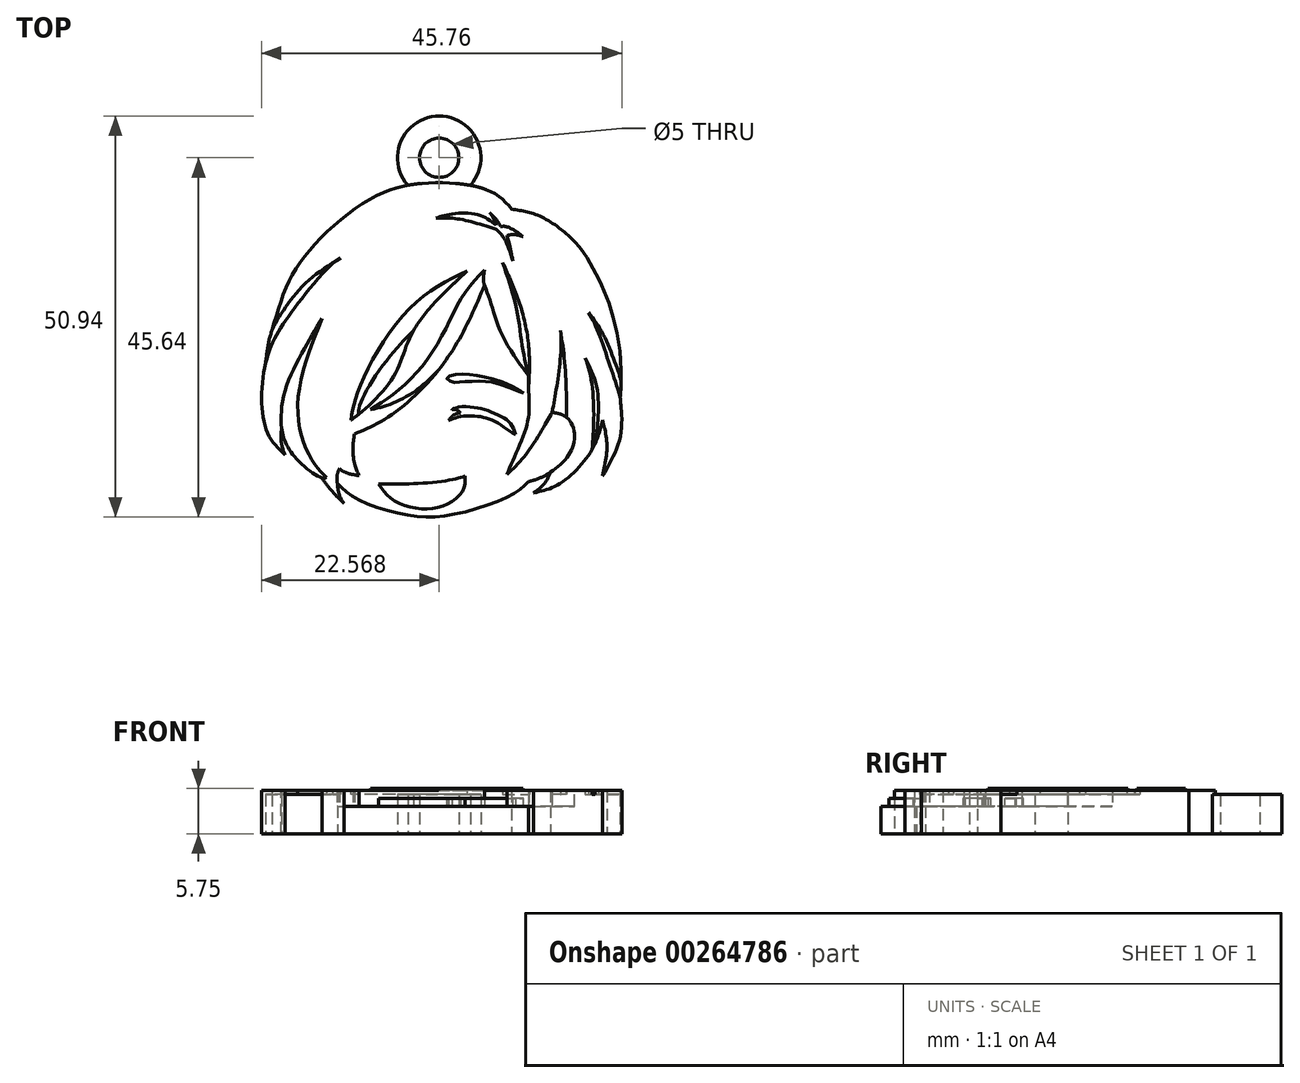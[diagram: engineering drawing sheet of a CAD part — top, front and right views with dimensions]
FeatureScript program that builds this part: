
annotation { "Feature Type Name" : "Feature", "Feature Type Description" : "" }
export const myFeature = defineFeature(function(context is Context, id is Id, definition is map)
    precondition{}
    {
        {
            var Q0;
            Q0=qCreatedBy(makeId("Top.planeOp"),FACE);
            var sketch = newSketch(context, id + "F0", { "sketchPlane" : qUnion([Q0])});
            skLineSegment(sketch, "E0", {"start": v(0, 25.68) * mm, "end": v(0, -14.32) * mm, "construction": true});
            skFitSpline(sketch, "E1", {"points": [v(-12.11, -11) * mm, v(-9.76, -12.87) * mm, v(-3.35, -15) * mm, v(2.65, -14.93) * mm, v(10, -12.46) * mm, v(12.18, -10.76) * mm], "startDerivative": vector(12.35, -12.38) * mm, "endDerivative": vector(10.78, 11.62) * mm});
            skFitSpline(sketch, "E2", {"points": [v(12.18, -10.76) * mm, v(14.09, -10.08) * mm, v(16.86, -7.95) * mm, v(18.04, -4.98) * mm, v(17, -2.6) * mm, v(15.17, -1.96) * mm], "startDerivative": vector(10.79, 2.75) * mm, "endDerivative": vector(-11.46, 1.84) * mm});
            skFitSpline(sketch, "E3", {"points": [v(15.17, -1.96) * mm, v(13.89, -4.19) * mm, v(11.42, -7.85) * mm, v(9.44, -9.83) * mm], "startDerivative": vector(-3.84, -6.82) * mm, "endDerivative": vector(-6.23, -5.5) * mm});
            skFitSpline(sketch, "E4", {"points": [v(-12.11, -11) * mm, v(-12.11, -9.83) * mm, v(-11.84, -9.1) * mm], "startDerivative": vector(-0.17, 2.25) * mm, "endDerivative": vector(0.73, 1.5) * mm});
            skFitSpline(sketch, "E5", {"points": [v(-11.84, -9.1) * mm, v(-11.03, -9.62) * mm, v(-9.33, -10) * mm], "startDerivative": vector(1.68, -1.34) * mm, "endDerivative": vector(3.28, -0.49) * mm});
            skFitSpline(sketch, "E6", {"points": [v(-9.33, -10) * mm, v(-9.85, -8.77) * mm, v(-10.14, -6.57) * mm, v(-9.93, -4.7) * mm], "startDerivative": vector(-1.97, 3.85) * mm, "endDerivative": vector(0.9, 5.24) * mm});
            skFitSpline(sketch, "E7", {"points": [v(-9.93, -4.7) * mm, v(-7.03, -3.4) * mm, v(-2.43, 0) * mm, v(2.7, 6.2) * mm, v(6.59, 14.18) * mm], "startDerivative": vector(15.57, 6.03) * mm, "endDerivative": vector(11.78, 27.65) * mm});
            skFitSpline(sketch, "E8", {"points": [v(6.59, 14.18) * mm, v(7.53, 11.45) * mm, v(9.07, 7.36) * mm, v(11.76, 3.27) * mm, v(12.18, 2.67) * mm], "startDerivative": vector(3.84, -10.5) * mm, "endDerivative": vector(1.51, -3.88) * mm});
            skFitSpline(sketch, "E9", {"points": [v(12.18, 2.67) * mm, v(12.18, 1.06) * mm, v(12.26, -1.4) * mm, v(11.85, -3.97) * mm, v(10.55, -7.25) * mm, v(9.44, -9.83) * mm], "startDerivative": vector(-0.17, -13.3) * mm, "endDerivative": vector(-4.42, -10.34) * mm});
            skFitSpline(sketch, "E10", {"points": [v(-12.11, -11) * mm, v(-11.84, -12.48) * mm, v(-11.26, -13.55) * mm], "startDerivative": vector(0.32, -2.98) * mm, "endDerivative": vector(1.41, -2.12) * mm});
            skFitSpline(sketch, "E11", {"points": [v(-11.26, -13.55) * mm, v(-13.1, -11.63) * mm, v(-14.07, -10.3) * mm], "startDerivative": vector(-3.59, 3.55) * mm, "endDerivative": vector(-1.98, 2.94) * mm});
            skFitSpline(sketch, "E12", {"points": [v(-14.05, 9.94) * mm, v(-16.53, 3.07) * mm, v(-17.07, -2.82) * mm, v(-15.88, -7.02) * mm, v(-14.56, -9.1) * mm, v(-13.47, -10.23) * mm], "startDerivative": vector(-10.57, -25.7) * mm, "endDerivative": vector(8.74, -8.35) * mm});
            skFitSpline(sketch, "E13", {"points": [v(-13.47, -10.23) * mm, v(-14.07, -10.3) * mm, v(-17.06, -8.13) * mm, v(-18.78, -5.57) * mm, v(-19.25, -3.19) * mm, v(-18.7, 0.95) * mm, v(-16.23, 6.25) * mm, v(-14.05, 9.94) * mm], "startDerivative": vector(-7.9, -3.21) * mm, "endDerivative": vector(12.69, 21.1) * mm});
            skFitSpline(sketch, "E14", {"points": [v(-19.19, -3.98) * mm, v(-19.27, -5.57) * mm, v(-18.78, -7.39) * mm], "startDerivative": vector(-0.4, -3.27) * mm, "endDerivative": vector(1.14, -3.48) * mm});
            skFitSpline(sketch, "E15", {"points": [v(-18.78, -7.39) * mm, v(-20.4, -5.57) * mm, v(-21.53, -2.66) * mm, v(-21.58, 2.24) * mm, v(-20.43, 6.68) * mm, v(-18.3, 10.23) * mm, v(-12.7, 16.96) * mm], "startDerivative": vector(-13.06, 14.6) * mm, "endDerivative": vector(30.17, 28.96) * mm});
            skFitSpline(sketch, "E16", {"points": [v(-12.7, 16.96) * mm, v(-11.7, 17.65) * mm], "startDerivative": vector(1, 0.69) * mm, "endDerivative": vector(1, 0.69) * mm});
            skFitSpline(sketch, "E17", {"points": [v(-11.7, 17.65) * mm, v(-16.11, 14.49) * mm, v(-18.94, 11) * mm, v(-20.52, 8.12) * mm, v(-21.21, 4.3) * mm], "startDerivative": vector(-16.65, -10.4) * mm, "endDerivative": vector(-1.83, -16.87) * mm});
            skFitSpline(sketch, "E18", {"points": [v(-20.38, 8.5) * mm, v(-18.48, 14.22) * mm, v(-15.07, 19.27) * mm, v(-8.42, 24.86) * mm, v(-2.6, 26.98) * mm, v(3.7, 27.04) * mm, v(7.93, 25.8) * mm, v(10.05, 23.86) * mm], "startDerivative": vector(11.29, 40.08) * mm, "endDerivative": vector(18.3, -20.86) * mm});
            skFitSpline(sketch, "E19", {"points": [v(10.05, 23.86) * mm, v(13.67, 22.93) * mm, v(18.22, 19.5) * mm, v(20.87, 15.37) * mm, v(22.83, 10.48) * mm, v(23.82, 0) * mm], "startDerivative": vector(22, -3.37) * mm, "endDerivative": vector(-4.69, -45.16) * mm});
            skFitSpline(sketch, "E20", {"points": [v(15, -9.56) * mm, v(14.09, -11.14) * mm, v(12.83, -12.19) * mm], "startDerivative": vector(-1.55, -3.32) * mm, "endDerivative": vector(-2.78, -1.93) * mm});
            skFitSpline(sketch, "E21", {"points": [v(12.83, -12.19) * mm, v(16.19, -11) * mm, v(20.25, -6.66) * mm, v(21.57, -2.95) * mm], "startDerivative": vector(10.98, 2.3) * mm, "endDerivative": vector(2.75, 11.42) * mm});
            skFitSpline(sketch, "E22", {"points": [v(21.57, -2.95) * mm, v(22.13, -6.17) * mm, v(21.57, -10.08) * mm], "startDerivative": vector(1.7, -6.59) * mm, "endDerivative": vector(-1.66, -7.64) * mm});
            skFitSpline(sketch, "E23", {"points": [v(5.07, 16.64) * mm, v(-2.43, 8.44) * mm, v(-5, 2.57) * mm, v(-10.38, -2.95) * mm, v(-14.16, -5.13) * mm], "startDerivative": vector(-29, -26.73) * mm, "endDerivative": vector(-18.26, -9.03) * mm});
            skFitSpline(sketch, "E24", {"points": [v(-14.16, -5.13) * mm, v(-11.64, -5.13) * mm, v(-9.93, -4.7) * mm], "startDerivative": vector(4.87, -0.26) * mm, "endDerivative": vector(3.55, 1.17) * mm});
            skFitSpline(sketch, "E25", {"points": [v(-2.43, 8.44) * mm, v(-4.37, 6.4) * mm, v(-8.03, 1.5) * mm, v(-9.36, -1.47) * mm, v(-9.44, -2.24) * mm], "startDerivative": vector(-7.12, -7.14) * mm, "endDerivative": vector(-0.06, -5.2) * mm});
            skFitSpline(sketch, "E26", {"points": [v(16.06, 10.25) * mm, v(16.3, 6.6) * mm, v(15.81, 1.7) * mm, v(15.17, -1.96) * mm], "startDerivative": vector(1.27, -11.01) * mm, "endDerivative": vector(-2.04, -10.92) * mm});
            skFitSpline(sketch, "E27", {"points": [v(17, -2.6) * mm, v(17, -0.67) * mm, v(16.78, 4.23) * mm, v(16.25, 8.44) * mm], "startDerivative": vector(0.07, 6.87) * mm, "endDerivative": vector(-1.64, 10.96) * mm});
            skFitSpline(sketch, "E28", {"points": [v(23.82, 0) * mm, v(22.51, 4) * mm, v(20.95, 8.44) * mm, v(19.8, 10.74) * mm], "startDerivative": vector(-3.08, 11) * mm, "endDerivative": vector(-4.1, 7.49) * mm});
            skFitSpline(sketch, "E29", {"points": [v(19.8, 10.74) * mm, v(21.57, 8.1) * mm, v(23.16, 4.36) * mm, v(23.95, 2.03) * mm], "startDerivative": vector(5.44, -7.3) * mm, "endDerivative": vector(1.84, -7.43) * mm});
            skFitSpline(sketch, "E30", {"points": [v(8.87, 17.05) * mm, v(10.55, 11.64) * mm, v(11.4, 6.35) * mm, v(12.18, 2.67) * mm], "startDerivative": vector(5.33, -14.86) * mm, "endDerivative": vector(2.88, -11.93) * mm});
            skFitSpline(sketch, "E31", {"points": [v(8.87, 17.05) * mm, v(10.87, 12.37) * mm, v(12.18, 6.63) * mm, v(12.18, 1.06) * mm], "startDerivative": vector(6.63, -14.09) * mm, "endDerivative": vector(-0.84, -16.47) * mm});
            skFitSpline(sketch, "E32", {"points": [v(18.48, 6.7) * mm, v(19.8, 3.68) * mm, v(20.46, -1.96) * mm, v(20.25, -6.66) * mm], "startDerivative": vector(5.18, -9.46) * mm, "endDerivative": vector(-1.03, -13.13) * mm});
            skFitSpline(sketch, "E33", {"points": [v(4.37, 15.98) * mm, v(-3.02, 11.16) * mm, v(-9.36, 1.06) * mm, v(-10.38, -2.95) * mm], "startDerivative": vector(-21.56, -10.26) * mm, "endDerivative": vector(-2.26, -14.44) * mm});
            skFitSpline(sketch, "E34", {"points": [v(6.59, 14.18) * mm, v(6.45, 14.79) * mm, v(6.59, 16.15) * mm], "startDerivative": vector(-0.47, 1.35) * mm, "endDerivative": vector(0.42, 2.5) * mm});
            skFitSpline(sketch, "E35", {"points": [v(6.59, 16.15) * mm, v(3.98, 13.05) * mm, v(1.6, 8.58) * mm, v(-1.53, 3.65) * mm, v(-5.07, 0.3) * mm, v(-7.86, -1.63) * mm], "startDerivative": vector(-14.68, -15.38) * mm, "endDerivative": vector(-15.93, -10.28) * mm});
            skFitSpline(sketch, "E36", {"points": [v(-7.86, -1.63) * mm, v(-4.86, -0.72) * mm, v(-1.67, 1.17) * mm, v(0.73, 3.41) * mm], "startDerivative": vector(9.28, 2.26) * mm, "endDerivative": vector(6.78, 7.07) * mm});
            skFitSpline(sketch, "E37", {"points": [v(8.06, 21.84) * mm, v(5.77, 23.14) * mm, v(2.15, 23.2) * mm, v(0.21, 22.64) * mm], "startDerivative": vector(-6.2, 4.74) * mm, "endDerivative": vector(-5.99, -2.2) * mm});
            skFitSpline(sketch, "E38", {"points": [v(0.4, 22.7) * mm, v(3.04, 22.64) * mm, v(8, 21.34) * mm], "startDerivative": vector(5.84, 0.26) * mm, "endDerivative": vector(9.18, -2.82) * mm});
            skFitSpline(sketch, "E39", {"points": [v(8, 21.34) * mm, v(9.07, 20.14) * mm, v(10.18, 17.28) * mm], "startDerivative": vector(2.67, -2.44) * mm, "endDerivative": vector(1.73, -5.52) * mm});
            skFitSpline(sketch, "E40", {"points": [v(10.18, 17.28) * mm, v(9.71, 19.49) * mm, v(9.43, 20.49) * mm], "startDerivative": vector(-0.82, 4.07) * mm, "endDerivative": vector(-0.69, 2.22) * mm});
            skFitSpline(sketch, "E41", {"points": [v(9.43, 20.49) * mm, v(10.33, 20.64) * mm, v(11.45, 20.36) * mm], "startDerivative": vector(1.88, 0.5) * mm, "endDerivative": vector(2.16, -0.73) * mm});
            skFitSpline(sketch, "E42", {"points": [v(8.64, 21.65) * mm, v(9.43, 21.61) * mm, v(10.87, 20.85) * mm, v(11.45, 20.36) * mm], "startDerivative": vector(2.43, 0.26) * mm, "endDerivative": vector(1.67, -1.54) * mm});
            skFitSpline(sketch, "E43", {"points": [v(8.06, 21.84) * mm, v(7.74, 22.64) * mm, v(7.25, 23.4) * mm], "startDerivative": vector(-0.6, 1.63) * mm, "endDerivative": vector(-1.03, 1.5) * mm});
            skFitSpline(sketch, "E44", {"points": [v(7.25, 23.4) * mm, v(8.22, 22.33) * mm, v(8.64, 21.65) * mm], "startDerivative": vector(1.9, -1.95) * mm, "endDerivative": vector(0.83, -1.54) * mm});
            skFitSpline(sketch, "E45", {"points": [v(6.59, 16.15) * mm, v(4.45, 15.54) * mm, v(2.54, 14.27) * mm], "startDerivative": vector(-4.44, -0.9) * mm, "endDerivative": vector(-3.63, -2.88) * mm});
            skLineSegment(sketch, "E46", {"start": v(5.07, 16.64) * mm, "end": v(-6.25, 25.97) * mm});
            skLineSegment(sketch, "E47", {"start": v(11.74, 9.35) * mm, "end": v(16.06, 21.48) * mm});
            skFitSpline(sketch, "E48", {"points": [v(23.82, 0) * mm, v(23.88, -0.74) * mm, v(23.89, -4.73) * mm, v(21.57, -10.08) * mm], "startDerivative": vector(0.4, -7.14) * mm, "endDerivative": vector(-6.66, -11.4) * mm});
            skFitSpline(sketch, "E49", {"points": [v(16.06, 10.25) * mm, v(17.69, 8.1) * mm, v(18.48, 6.7) * mm], "startDerivative": vector(3.19, -3.97) * mm, "endDerivative": vector(1.58, -3.1) * mm});
            skFitSpline(sketch, "E50", {"points": [v(19.36, 4.94) * mm, v(20.77, 1.57) * mm, v(21, -2.9) * mm, v(20.59, -6) * mm], "startDerivative": vector(5.07, -9.54) * mm, "endDerivative": vector(-1.62, -9.52) * mm});
            skSolve(sketch);
        }
        {
            var Q0;
            Q0=makeQuery(id+"F0.imprint","IMPRINT",FACE,{"disambiguationData":[TD([[makeQuery(id+"F0.imprint","IMPRINT",EDGE,{"derivedFrom":sQuery(id+"F0.wireOp",EDGE,"E1")}),1.0]])]});
            var Q1;
            {var subQ0=sQuery(id+"F0.wireOp",EDGE,"E25");Q1=makeQuery(id+"F0.imprint","IMPRINT",FACE,{"disambiguationData":[TD([[makeQuery(id+"F0.imprint","IMPRINT",EDGE,{"derivedFrom":subQ0}),1.0]])]});}
            extrude(context, id + "F1", {"entities" : qUnion([Q0, Q1]), "depth" : 3.5 * mm, "offsetDistance" : 25 * mm});
        }
        {
            var Q0;
            {var subQ3=sQuery(id+"F0.wireOp",EDGE,"E27");Q0=makeQuery(id+"F0.imprint","IMPRINT",FACE,{"disambiguationData":[TD([[makeQuery(id+"F0.imprint","IMPRINT",EDGE,{"derivedFrom":subQ3}),1.0]])]});}
            var Q1;
            Q1=makeQuery(id+"F0.imprint","IMPRINT",FACE,{"disambiguationData":[TD([[makeQuery(id+"F0.imprint","IMPRINT",EDGE,{"derivedFrom":sQuery(id+"F0.wireOp",EDGE,"E32")}),1.0]])]});
            var Q2;
            {var subQ0=sQuery(id+"F0.wireOp",EDGE,"E28");Q2=makeQuery(id+"F0.imprint","IMPRINT",FACE,{"disambiguationData":[TD([[makeQuery(id+"F0.imprint","IMPRINT",EDGE,{"derivedFrom":subQ0}),-1.0]])]});}
            var Q3;
            {var subQ0=sQuery(id+"F0.wireOp",EDGE,"E12");Q3=makeQuery(id+"F0.imprint","IMPRINT",FACE,{"disambiguationData":[TD([[makeQuery(id+"F0.imprint","IMPRINT",EDGE,{"derivedFrom":subQ0}),-1.0]])]});}
            var Q4;
            {var subQ0=sQuery(id+"F0.wireOp",EDGE,"E16");Q4=makeQuery(id+"F0.imprint","IMPRINT",FACE,{"disambiguationData":[TD([[makeQuery(id+"F0.imprint","IMPRINT",EDGE,{"derivedFrom":subQ0}),1.0]])]});}
            var Q5;
            {var subQ0=sQuery(id+"F0.wireOp",EDGE,"E25");Q5=makeQuery(id+"F0.imprint","IMPRINT",FACE,{"disambiguationData":[TD([[makeQuery(id+"F0.imprint","IMPRINT",EDGE,{"derivedFrom":subQ0}),-1.0]])]});}
            var Q6;
            {var subQ0=sQuery(id+"F0.wireOp",EDGE,"E30");Q6=makeQuery(id+"F0.imprint","IMPRINT",FACE,{"disambiguationData":[TD([[makeQuery(id+"F0.imprint","IMPRINT",EDGE,{"derivedFrom":subQ0}),1.0]])]});}
            extrude(context, id + "F2", {"entities" : qUnion([Q0, Q1, Q2, Q3, Q4, Q5, Q6]), "operationType" : NewBodyOperationType.ADD, "depth" : 5 * mm, "offsetDistance" : 25 * mm});
        }
        {
            var Q0;
            {var subQ0=sQuery(id+"F0.wireOp",EDGE,"E34");Q0=makeQuery(id+"F0.imprint","IMPRINT",FACE,{"disambiguationData":[TD([[makeQuery(id+"F0.imprint","IMPRINT",EDGE,{"derivedFrom":subQ0}),1.0]])]});}
            extrude(context, id + "F3", {"entities" : qUnion([Q0]), "operationType" : NewBodyOperationType.ADD, "depth" : 5.75 * mm, "offsetDistance" : 25 * mm});
        }
        {
            var Q0;
            {var subQ6=sQuery(id+"F0.wireOp",EDGE,"E24");Q0=makeQuery(id+"F0.imprint","IMPRINT",FACE,{"disambiguationData":[TD([[makeQuery(id+"F0.imprint","IMPRINT",EDGE,{"derivedFrom":subQ6}),1.0]])]});}
            extrude(context, id + "F4", {"entities" : qUnion([Q0]), "depth" : 5.5 * mm, "offsetDistance" : 25 * mm});
        }
        {
            var Q0;
            {var subQ0=sQuery(id+"F0.wireOp",EDGE,"E38");Q0=makeQuery(id+"F0.imprint","IMPRINT",FACE,{"disambiguationData":[TD([[makeQuery(id+"F0.imprint","IMPRINT",EDGE,{"derivedFrom":subQ0}),1.0]])]});}
            extrude(context, id + "F5", {"entities" : qUnion([Q0]), "operationType" : NewBodyOperationType.ADD, "depth" : 5.75 * mm, "offsetDistance" : 25 * mm});
        }
        {
            var Q0;
            Q0=makeQuery(id+"F0.imprint","IMPRINT",FACE,{"disambiguationData":[TD([[makeQuery(id+"F0.imprint","IMPRINT",EDGE,{"derivedFrom":sQuery(id+"F0.wireOp",EDGE,"E4")}),1.0]])]});
            extrude(context, id + "F6", {"entities" : qUnion([Q0]), "operationType" : NewBodyOperationType.ADD, "depth" : 5.5 * mm, "offsetDistance" : 25 * mm});
        }
        {
            var Q0;
            Q0=makeQuery(id+"F0.imprint","IMPRINT",FACE,{"disambiguationData":[TD([[makeQuery(id+"F0.imprint","IMPRINT",EDGE,{"derivedFrom":sQuery(id+"F0.wireOp",EDGE,"E8")}),1.0]])]});
            extrude(context, id + "F7", {"entities" : qUnion([Q0]), "operationType" : NewBodyOperationType.ADD, "depth" : 5.5 * mm, "offsetDistance" : 25 * mm});
        }
        {
            var Q0;
            {var subQ4=sQuery(id+"F0.wireOp",EDGE,"E3");Q0=makeQuery(id+"F0.imprint","IMPRINT",FACE,{"disambiguationData":[TD([[makeQuery(id+"F0.imprint","IMPRINT",EDGE,{"derivedFrom":subQ4}),-1.0]])]});}
            extrude(context, id + "F8", {"entities" : qUnion([Q0]), "operationType" : NewBodyOperationType.ADD, "depth" : 5.5 * mm, "offsetDistance" : 25 * mm});
        }
        {
            var Q0;
            {var subQ1=sQuery(id+"F0.wireOp",EDGE,"E20");Q0=makeQuery(id+"F0.imprint","IMPRINT",FACE,{"disambiguationData":[TD([[makeQuery(id+"F0.imprint","IMPRINT",EDGE,{"derivedFrom":subQ1}),1.0]])]});}
            extrude(context, id + "F9", {"entities" : qUnion([Q0]), "operationType" : NewBodyOperationType.ADD, "depth" : 5.5 * mm, "offsetDistance" : 25 * mm});
        }
        {
            var Q0;
            Q0=qCreatedBy(makeId("Top.planeOp"),FACE);
            var sketch = newSketch(context, id + "F10", { "sketchPlane" : qUnion([Q0])});
            skFitSpline(sketch, "E51", {"points": [v(-6.88, -11.06) * mm, v(-3.04, -11.06) * mm, v(2.25, -10.56) * mm, v(4.14, -10.06) * mm], "startDerivative": vector(10.2, -0.25) * mm, "endDerivative": vector(6.46, 2.11) * mm});
            skFitSpline(sketch, "E52", {"points": [v(-6.88, -11.06) * mm, v(-5.13, -13) * mm, v(-1.7, -14.2) * mm, v(1.75, -13.7) * mm, v(3.84, -11.86) * mm, v(4.14, -10.06) * mm], "startDerivative": vector(7.65, -10.93) * mm, "endDerivative": vector(0.06, 11.32) * mm});
            skFitSpline(sketch, "E53", {"points": [v(3.53, -2.02) * mm, v(2.77, -2.23) * mm, v(2.02, -2.98) * mm], "startDerivative": vector(-1.69, -0.24) * mm, "endDerivative": vector(-1.34, -1.66) * mm});
            skFitSpline(sketch, "E54", {"points": [v(2.02, -2.98) * mm, v(3.57, -2.5) * mm, v(5.48, -2.44) * mm, v(7.61, -2.98) * mm, v(10.15, -4.6) * mm], "startDerivative": vector(6.93, 2.62) * mm, "endDerivative": vector(8.63, -6.27) * mm});
            skFitSpline(sketch, "E55", {"points": [v(3.53, -2.02) * mm, v(2.96, -1.62) * mm, v(2.44, -1.64) * mm], "startDerivative": vector(-1.04, 0.96) * mm, "endDerivative": vector(-1.14, -0.23) * mm});
            skFitSpline(sketch, "E56", {"points": [v(2.44, -1.64) * mm, v(3.27, -1.3) * mm, v(5.43, -1.35) * mm, v(7.28, -1.85) * mm, v(9.02, -2.67) * mm, v(9.92, -3.44) * mm, v(10.55, -4.8) * mm], "startDerivative": vector(5.57, 3.15) * mm, "endDerivative": vector(3.4, -9.15) * mm});
            skFitSpline(sketch, "E57", {"points": [v(10.15, -4.6) * mm, v(10.55, -4.8) * mm], "startDerivative": vector(0.4, -0.2) * mm, "endDerivative": vector(0.4, -0.2) * mm});
            skFitSpline(sketch, "E58", {"points": [v(11.5, 0.5) * mm, v(8.85, 1.91) * mm, v(5.23, 2.74) * mm, v(2.82, 2.83) * mm, v(1.82, 2.33) * mm, v(2.52, 1.87) * mm, v(3.69, 1.91) * mm, v(5.98, 2) * mm, v(8.35, 1.66) * mm, v(11.5, 0.5) * mm]});
            skSolve(sketch);
        }
        {
            var Q0;
            Q0 = qSketchRegion(id + "F10", true);
            extrude(context, id + "F11", {"entities" : qUnion([Q0]), "operationType" : NewBodyOperationType.ADD, "depth" : 4.5 * mm, "offsetDistance" : 25 * mm});
        }
        {
            var Q0;
            Q0=qCreatedBy(makeId("Top.planeOp"),FACE);
            var sketch = newSketch(context, id + "F12", { "sketchPlane" : qUnion([Q0])});
            skCircle(sketch, "E59", {"center": v(0.83, 30.38) * mm, "radius": 5.3 * mm});
            skCircle(sketch, "E60", {"center": v(0.83, 30.38) * mm, "radius": 2.5 * mm});
            skLineSegment(sketch, "E61", {"start": v(-1.67, 30.38) * mm, "end": v(3.33, 30.38) * mm, "construction": true});
            skSolve(sketch);
        }
        {
            var Q0;
            Q0=makeQuery(id+"F12.imprint","IMPRINT",FACE,{"disambiguationData":[TD([[makeQuery(id+"F12.imprint","IMPRINT",EDGE,{"derivedFrom":sQuery(id+"F12.wireOp",EDGE,"E59")}),1.0]])]});
            extrude(context, id + "F13", {"entities" : qUnion([Q0]), "operationType" : NewBodyOperationType.ADD, "depth" : 5 * mm, "offsetDistance" : 25 * mm});
        }
    });
